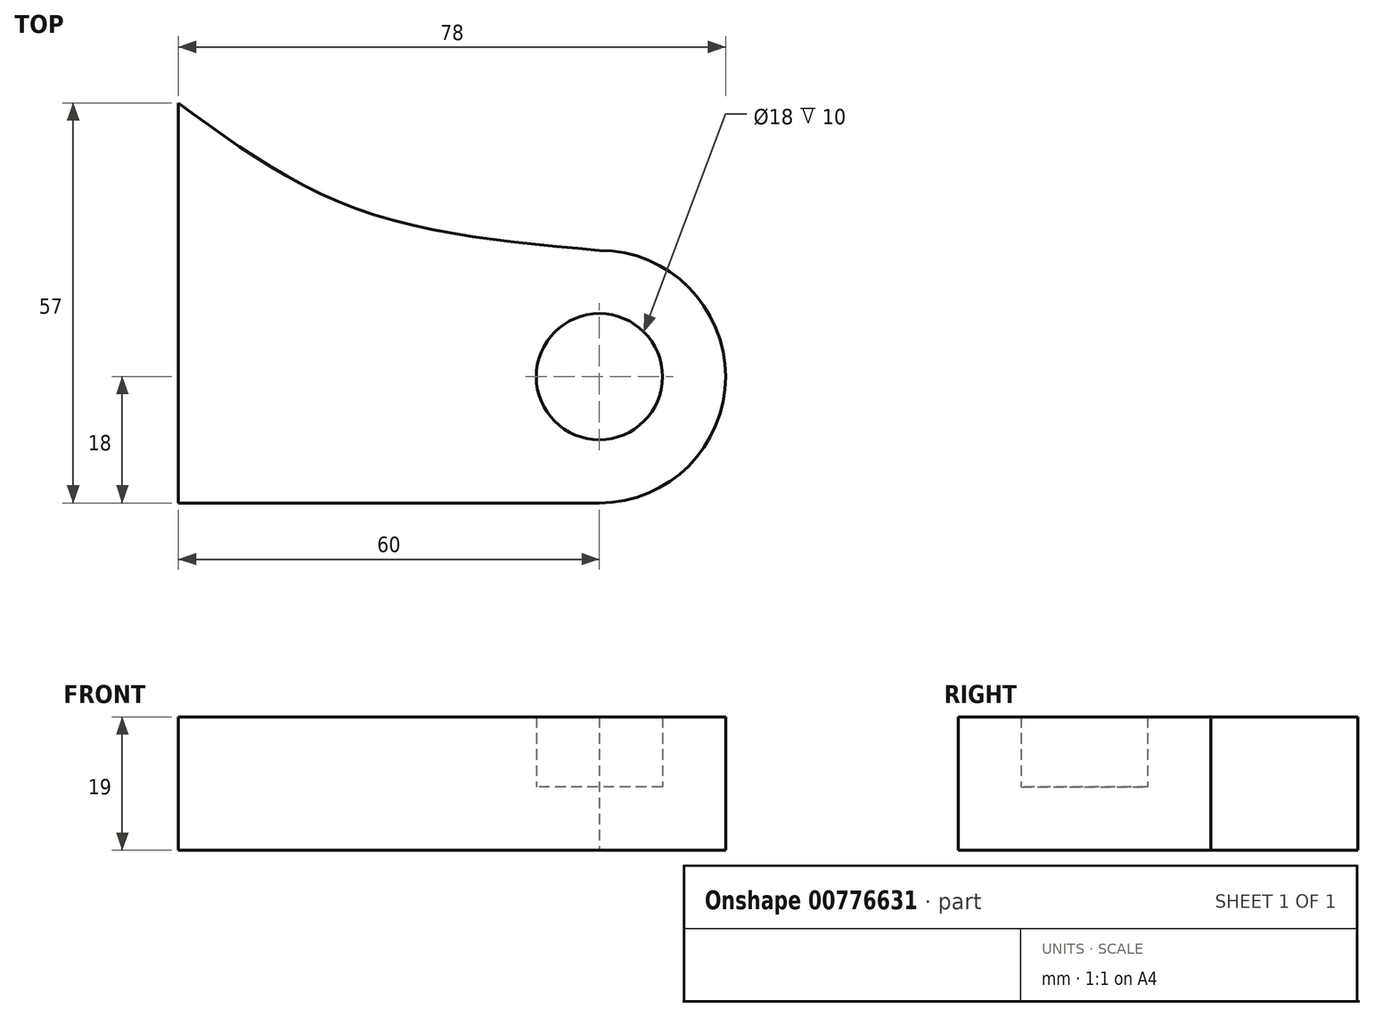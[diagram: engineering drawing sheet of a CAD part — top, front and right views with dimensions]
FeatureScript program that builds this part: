
annotation { "Feature Type Name" : "Feature", "Feature Type Description" : "" }
export const myFeature = defineFeature(function(context is Context, id is Id, definition is map)
    precondition{}
    {
        {
            var Q0;
            Q0=qCreatedBy(makeId("Top.planeOp"),FACE);
            var sketch = newSketch(context, id + "F0", { "sketchPlane" : qUnion([Q0])});
            skArc(sketch, "E0", {"start": v(0, -18) * mm, "mid": v(18, 0) * mm, "end": v(0, 18) * mm});
            skPoint(sketch, "E1", {"position": v(18, 0) * mm});
            skLineSegment(sketch, "E2", {"start": v(18, 70.6) * mm, "end": v(-60, 70.6) * mm});
            skPoint(sketch, "E3", {"position": v(0, -18) * mm});
            skLineSegment(sketch, "E4", {"start": v(0, -18) * mm, "end": v(-60, -18) * mm});
            skLineSegment(sketch, "E5", {"start": v(-60, -18) * mm, "end": v(-60, 39) * mm});
            skFitSpline(sketch, "E6", {"points": [v(-60, 39) * mm, v(-34.79, 23.99) * mm, v(0, 18) * mm], "startDerivative": vector(49.61, -36.26) * mm, "endDerivative": vector(70.07, -6.2) * mm});
            skSolve(sketch);
        }
        {
            var Q0;
            Q0=makeQuery(id+"F0.imprint","IMPRINT",FACE,{"disambiguationData":[TD([[makeQuery(id+"F0.imprint","IMPRINT",EDGE,{"derivedFrom":sQuery(id+"F0.wireOp",EDGE,"E0")}),1.0]])]});
            extrude(context, id + "F1", {"entities" : qUnion([Q0]), "depth" : 19 * mm, "offsetDistance" : 25.4 * mm});
        }
        {
            var Q0;
            Q0=makeQuery(id+"F1.opExtrude","CAP_FACE",FACE,{"disambiguationData":[OSD([sQuery(id+"F0.wireOp",EDGE,"E0"),sQuery(id+"F0.wireOp",EDGE,"E4"),sQuery(id+"F0.wireOp",EDGE,"E5"),sQuery(id+"F0.wireOp",EDGE,"E6")])],"isStart":false});
            var sketch = newSketch(context, id + "F2", { "sketchPlane" : qUnion([Q0])});
            skCircle(sketch, "E7", {"center": v(0, 0) * mm, "radius": 9 * mm});
            skSolve(sketch);
        }
        {
            var Q0;
            Q0=makeQuery(id+"F2.imprint","IMPRINT",FACE,{"disambiguationData":[TD([[makeQuery(id+"F2.imprint","IMPRINT",EDGE,{"derivedFrom":sQuery(id+"F2.wireOp",EDGE,"E7")}),1.0]])]});
            extrude(context, id + "F3", {"entities" : qUnion([Q0]), "operationType" : NewBodyOperationType.REMOVE, "depth" : 25.4 * mm, "offsetDistance" : 25.4 * mm, "hasSecondDirection" : true, "secondDirectionOppositeDirection" : true, "secondDirectionDepth" : 10 * mm});
        }
    });
